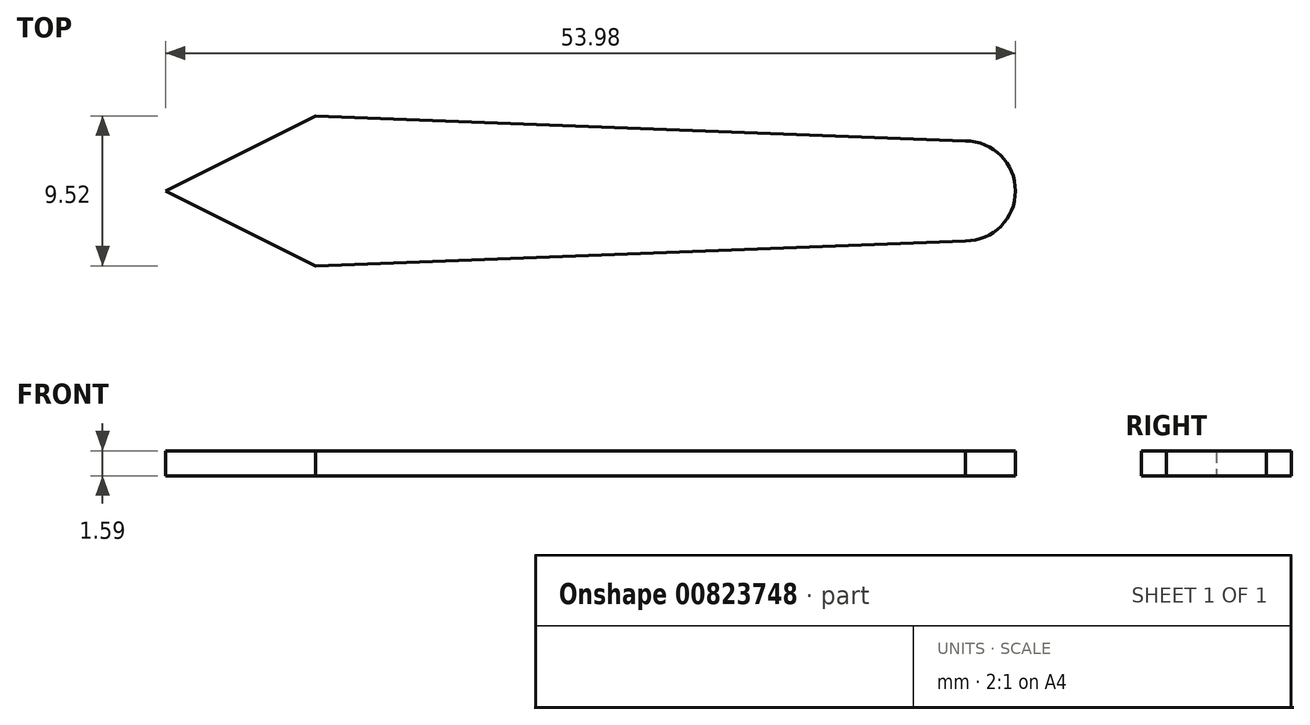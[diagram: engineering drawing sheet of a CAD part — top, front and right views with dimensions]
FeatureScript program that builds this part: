
annotation { "Feature Type Name" : "Feature", "Feature Type Description" : "" }
export const myFeature = defineFeature(function(context is Context, id is Id, definition is map)
    precondition{}
    {
        {
            var Q0;
            Q0=qCreatedBy(makeId("Top.planeOp"),FACE);
            var sketch = newSketch(context, id + "F0", { "sketchPlane" : qUnion([Q0])});
            skCircle(sketch, "E0", {"center": v(0, 0) * mm, "radius": 3.18 * mm});
            skLineSegment(sketch, "E1", {"start": v(0, 0) * mm, "end": v(-50.8, 0) * mm});
            skLineSegment(sketch, "E2", {"start": v(-50.8, 0) * mm, "end": v(-41.28, 4.76) * mm});
            skLineSegment(sketch, "E3", {"start": v(-41.28, 4.76) * mm, "end": v(0, 3.18) * mm});
            skLineSegment(sketch, "E4.MirrorCS", {"start": v(-50.8, 0) * mm, "end": v(-41.28, -4.76) * mm});
            skLineSegment(sketch, "E5.MirrorCS", {"start": v(-41.28, -4.76) * mm, "end": v(0, -3.17) * mm});
            skSolve(sketch);
        }
        {
            var Q0;
            {var subQ4=sQuery(id+"F0.wireOp",EDGE,"E2");Q0=makeQuery(id+"F0.imprint","IMPRINT",FACE,{"disambiguationData":[TD([[makeQuery(id+"F0.imprint","IMPRINT",EDGE,{"derivedFrom":subQ4}),-1.0]])]});}
            var Q1;
            {var subQ0=sQuery(id+"F0.wireOp",EDGE,"E0");var subQ1=makeQuery(id+"F0.imprint","INTERSECT",VERTEX,{"derivedFrom":[subQ0,sQuery(id+"F0.wireOp",EDGE,"E3")]});Q1=makeQuery(id+"F0.imprint","IMPRINT",FACE,{"disambiguationData":[TD([[makeQuery(id+"F0.imprint","IMPRINT",EDGE,{"disambiguationData":[TD([[subQ1,-1.0]])],"derivedFrom":subQ0}),1.0]])]});}
            var Q2;
            {var subQ4=sQuery(id+"F0.wireOp",EDGE,"E4.MirrorCS");Q2=makeQuery(id+"F0.imprint","IMPRINT",FACE,{"disambiguationData":[TD([[makeQuery(id+"F0.imprint","IMPRINT",EDGE,{"derivedFrom":subQ4}),1.0]])]});}
            extrude(context, id + "F1", {"entities" : qUnion([Q0, Q1, Q2]), "depth" : 1.59 * mm, "offsetDistance" : 25.4 * mm});
        }
        {
            var Q0;
            Q0=makeQuery(id+"F1.opExtrude","SWEPT_BODY",BODY,{"disambiguationData":[OSD([sQuery(id+"F0.wireOp",EDGE,"E0"),sQuery(id+"F0.wireOp",EDGE,"E2"),sQuery(id+"F0.wireOp",EDGE,"E3"),sQuery(id+"F0.wireOp",EDGE,"E4.MirrorCS"),sQuery(id+"F0.wireOp",EDGE,"E5.MirrorCS")])]});
            transform(context, id + "F2", {"entities" : qUnion([Q0]), "transformType" : TransformType.TRANSLATION_3D, "dx" : 0 * mm, "dy" : 0 * mm, "dz" : 0 * mm, "makeCopy" : true});
        }
        {
            var Q0;
            Q0=makeQuery(id+"F2.opPattern","COPY",BODY,{"derivedFrom":makeQuery(id+"F1.opExtrude","SWEPT_BODY",BODY,{"disambiguationData":[OSD([sQuery(id+"F0.wireOp",EDGE,"E0"),sQuery(id+"F0.wireOp",EDGE,"E2"),sQuery(id+"F0.wireOp",EDGE,"E3"),sQuery(id+"F0.wireOp",EDGE,"E4.MirrorCS"),sQuery(id+"F0.wireOp",EDGE,"E5.MirrorCS")])]}),"instanceName":"1"});
            deleteBodies(context, id + "F3", {"entities" : qUnion([Q0])});
        }
    });
